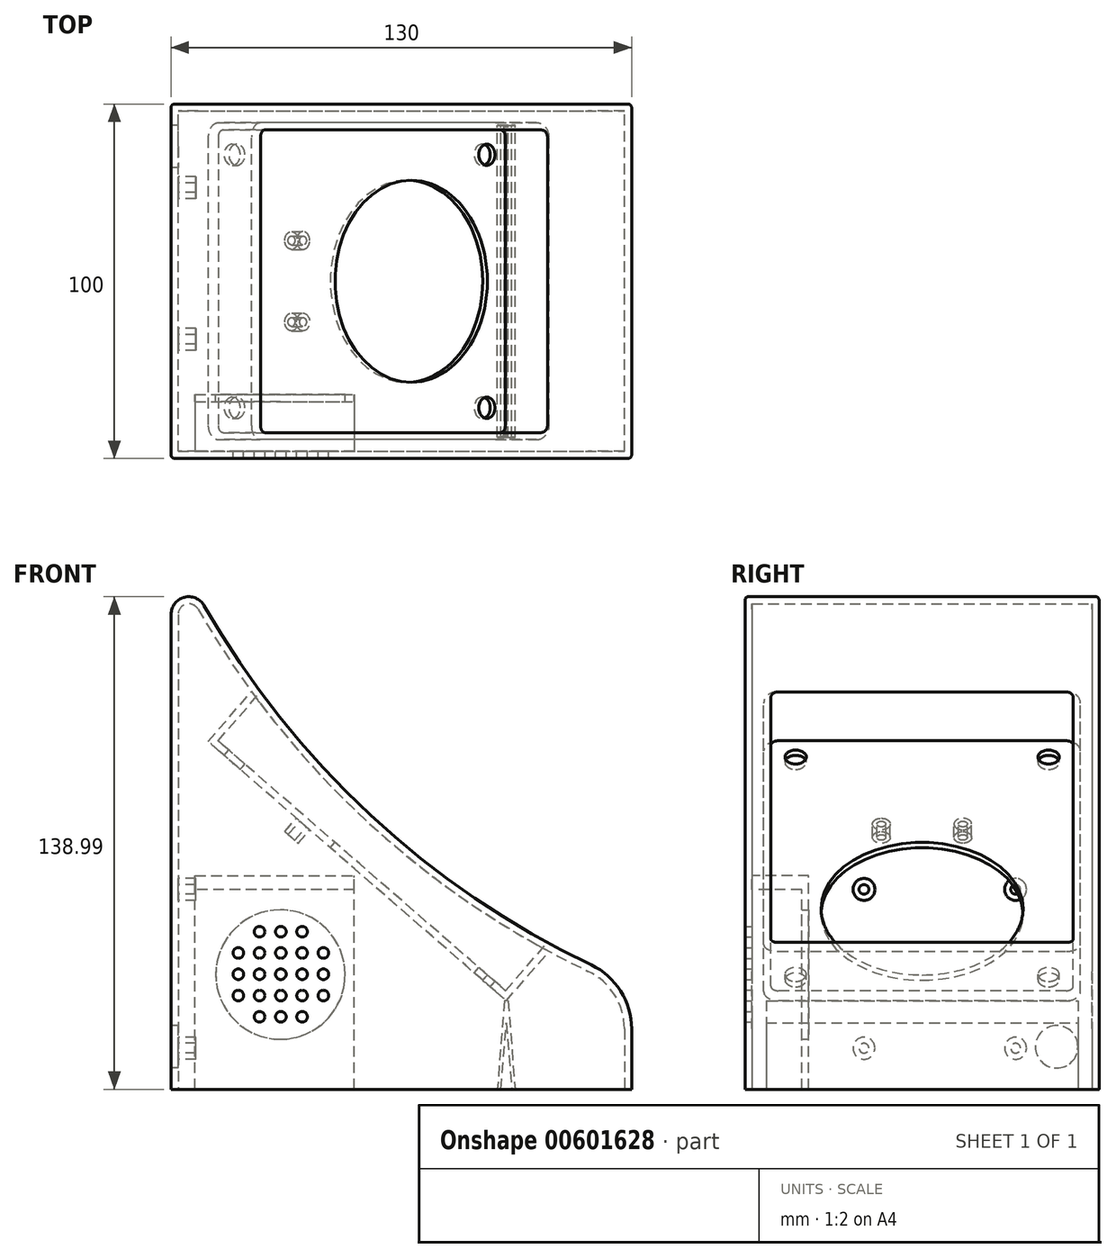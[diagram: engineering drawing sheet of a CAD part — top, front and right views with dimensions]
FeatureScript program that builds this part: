
annotation { "Feature Type Name" : "Feature", "Feature Type Description" : "" }
export const myFeature = defineFeature(function(context is Context, id is Id, definition is map)
    precondition{}
    {
        {
            var Q0;
            Q0=qCreatedBy(makeId("Front.planeOp"),FACE);
            var sketch = newSketch(context, id + "F0", { "sketchPlane" : qUnion([Q0])});
            skLineSegment(sketch, "E0", {"start": v(-84.02, -67.29) * mm, "end": v(45.98, -67.29) * mm});
            skPoint(sketch, "E1.visualSharp", {"position": v(-84.02, 87.14) * mm});
            skPoint(sketch, "E2.visualSharp", {"position": v(45.98, -37.29) * mm});
            skArc(sketch, "E3", {"start": v(-74.68, 69.19) * mm, "mid": v(-23.15, 5.98) * mm, "end": v(45.98, -37.29) * mm});
            skLineSegment(sketch, "E4", {"start": v(-84.02, 66.7) * mm, "end": v(-84.02, -67.29) * mm});
            skLineSegment(sketch, "E5", {"start": v(45.98, -37.29) * mm, "end": v(45.98, -67.29) * mm});
            skArc(sketch, "E6.filletArc", {"start": v(-74.68, 69.19) * mm, "mid": v(-80.3, 71.53) * mm, "end": v(-84.02, 66.7) * mm});
            skSolve(sketch);
        }
        {
            var Q0;
            Q0=makeQuery(id+"F0.imprint","IMPRINT",FACE,{"disambiguationData":[TD([[makeQuery(id+"F0.imprint","IMPRINT",EDGE,{"derivedFrom":sQuery(id+"F0.wireOp",EDGE,"E0")}),1.0]])]});
            extrude(context, id + "F1", {"entities" : qUnion([Q0]), "endBound" : BoundingType.SYMMETRIC, "depth" : 100 * mm});
        }
        {
            var Q0;
            Q0=makeQuery(id+"F1.opExtrude","SWEPT_EDGE",EDGE,{"disambiguationData":[OSD([sQuery(id+"F0.wireOp",EDGE,"E3"),sQuery(id+"F0.wireOp",EDGE,"E5")])]});
            cPlane(context, id + "F2", {"entities" : qUnion([Q0]), "cplaneType" : CPlaneType.LINE_ANGLE, "offset" : 25 * mm, "angle" : 41 * degree, "width" : 150 * mm, "height" : 150 * mm});
        }
        {
            var Q0;
            Q0=qCreatedBy(id+"F2.planeOp",FACE);
            var sketch = newSketch(context, id + "F3", { "sketchPlane" : qUnion([Q0])});
            skLineSegment(sketch, "E7.bottom", {"start": v(31.75, 42.7) * mm, "end": v(-71.75, 42.7) * mm});
            skLineSegment(sketch, "E7.top", {"start": v(31.75, -42.7) * mm, "end": v(-71.75, -42.7) * mm});
            skLineSegment(sketch, "E7.left", {"start": v(33.75, 40.7) * mm, "end": v(33.75, -40.7) * mm});
            skLineSegment(sketch, "E7.right", {"start": v(-73.75, 40.7) * mm, "end": v(-73.75, -40.7) * mm});
            skPoint(sketch, "E7.middle", {"position": v(-20, 0) * mm});
            skPoint(sketch, "E8.visualSharp", {"position": v(-73.75, -42.7) * mm});
            skArc(sketch, "E8.filletArc", {"start": v(-73.75, -40.7) * mm, "mid": v(-73.16, -42.11) * mm, "end": v(-71.75, -42.7) * mm});
            skPoint(sketch, "E9.visualSharp", {"position": v(-73.75, 42.7) * mm});
            skArc(sketch, "E9.filletArc", {"start": v(-71.75, 42.7) * mm, "mid": v(-73.16, 42.11) * mm, "end": v(-73.75, 40.7) * mm});
            skPoint(sketch, "E10.visualSharp", {"position": v(33.75, 42.7) * mm});
            skArc(sketch, "E10.filletArc", {"start": v(33.75, 40.7) * mm, "mid": v(33.16, 42.11) * mm, "end": v(31.75, 42.7) * mm});
            skPoint(sketch, "E11.visualSharp", {"position": v(33.75, -42.7) * mm});
            skArc(sketch, "E11.filletArc", {"start": v(31.75, -42.7) * mm, "mid": v(33.16, -42.11) * mm, "end": v(33.75, -40.7) * mm});
            skCircle(sketch, "E12", {"center": v(-1.55, 0) * mm, "radius": 28.5 * mm});
            skCircle(sketch, "E13", {"center": v(-66.75, -35.7) * mm, "radius": 3 * mm});
            skCircle(sketch, "E14", {"center": v(-66.75, 35.7) * mm, "radius": 3 * mm});
            skCircle(sketch, "E15", {"center": v(26.75, 35.7) * mm, "radius": 3 * mm});
            skCircle(sketch, "E16", {"center": v(26.75, -35.7) * mm, "radius": 3 * mm});
            skSolve(sketch);
        }
        {
            var Q0;
            Q0=makeQuery(id+"F3.imprint","IMPRINT",FACE,{"disambiguationData":[TD([[makeQuery(id+"F3.imprint","IMPRINT",EDGE,{"derivedFrom":sQuery(id+"F3.wireOp",EDGE,"E7.bottom")}),1.0]])]});
            var Q1;
            Q1=makeQuery(id+"F3.imprint","IMPRINT",FACE,{"disambiguationData":[TD([[makeQuery(id+"F3.imprint","IMPRINT",EDGE,{"derivedFrom":sQuery(id+"F3.wireOp",EDGE,"E12")}),1.0]])]});
            var Q2;
            Q2=makeQuery(id+"F3.imprint","IMPRINT",FACE,{"disambiguationData":[TD([[makeQuery(id+"F3.imprint","IMPRINT",EDGE,{"derivedFrom":sQuery(id+"F3.wireOp",EDGE,"E14")}),1.0]])]});
            var Q3;
            Q3=makeQuery(id+"F3.imprint","IMPRINT",FACE,{"disambiguationData":[TD([[makeQuery(id+"F3.imprint","IMPRINT",EDGE,{"derivedFrom":sQuery(id+"F3.wireOp",EDGE,"E15")}),1.0]])]});
            var Q4;
            Q4=makeQuery(id+"F3.imprint","IMPRINT",FACE,{"disambiguationData":[TD([[makeQuery(id+"F3.imprint","IMPRINT",EDGE,{"derivedFrom":sQuery(id+"F3.wireOp",EDGE,"E16")}),1.0]])]});
            var Q5;
            Q5=makeQuery(id+"F3.imprint","IMPRINT",FACE,{"disambiguationData":[TD([[makeQuery(id+"F3.imprint","IMPRINT",EDGE,{"derivedFrom":sQuery(id+"F3.wireOp",EDGE,"E13")}),1.0]])]});
            extrude(context, id + "F4", {"entities" : qUnion([Q0, Q1, Q2, Q3, Q4, Q5]), "operationType" : NewBodyOperationType.REMOVE, "oppositeDirection" : true, "depth" : 25 * mm});
        }
        {
            var Q0;
            Q0=makeQuery(id+"F1.opExtrude","SWEPT_EDGE",EDGE,{"disambiguationData":[OSD([sQuery(id+"F0.wireOp",EDGE,"E3"),sQuery(id+"F0.wireOp",EDGE,"E5")])]});
            fillet(context, id + "F5", {"entities" : qUnion([Q0]), "radius" : 20 * mm, "tangentPropagation" : true, "allowEdgeOverflow" : false});
        }
        {
            var Q0;
            Q0=makeQuery(id+"F1.opExtrude","SWEPT_FACE",FACE,{"disambiguationData":[OSD([sQuery(id+"F0.wireOp",EDGE,"E0")])]});
            shell(context, id + "F6", {"entities" : qUnion([Q0]), "thickness" : 2 * mm});
        }
        {
            var Q0;
            Q0=makeQuery(id+"F3.imprint","IMPRINT",FACE,{"disambiguationData":[TD([[makeQuery(id+"F3.imprint","IMPRINT",EDGE,{"derivedFrom":sQuery(id+"F3.wireOp",EDGE,"E12")}),1.0]])]});
            var Q1;
            Q1=makeQuery(id+"F3.imprint","IMPRINT",FACE,{"disambiguationData":[TD([[makeQuery(id+"F3.imprint","IMPRINT",EDGE,{"derivedFrom":sQuery(id+"F3.wireOp",EDGE,"E14")}),1.0]])]});
            var Q2;
            Q2=makeQuery(id+"F3.imprint","IMPRINT",FACE,{"disambiguationData":[TD([[makeQuery(id+"F3.imprint","IMPRINT",EDGE,{"derivedFrom":sQuery(id+"F3.wireOp",EDGE,"E13")}),1.0]])]});
            var Q3;
            Q3=makeQuery(id+"F3.imprint","IMPRINT",FACE,{"disambiguationData":[TD([[makeQuery(id+"F3.imprint","IMPRINT",EDGE,{"derivedFrom":sQuery(id+"F3.wireOp",EDGE,"E15")}),1.0]])]});
            var Q4;
            Q4=makeQuery(id+"F3.imprint","IMPRINT",FACE,{"disambiguationData":[TD([[makeQuery(id+"F3.imprint","IMPRINT",EDGE,{"derivedFrom":sQuery(id+"F3.wireOp",EDGE,"E16")}),1.0]])]});
            extrude(context, id + "F7", {"entities" : qUnion([Q0, Q1, Q2, Q3, Q4]), "operationType" : NewBodyOperationType.REMOVE, "oppositeDirection" : true, "depth" : 40 * mm});
        }
        {
            var Q0;
            Q0=makeQuery(id+"F1.opExtrude","SWEPT_FACE",FACE,{"disambiguationData":[OSD([sQuery(id+"F0.wireOp",EDGE,"E4")])]});
            var sketch = newSketch(context, id + "F8", { "sketchPlane" : qUnion([Q0])});
            skCircle(sketch, "E17", {"center": v(0, 42.55) * mm, "radius": 25 * mm, "construction": true});
            skLineSegment(sketch, "E18", {"start": v(0, 0) * mm, "end": v(0, -62.03) * mm, "construction": true});
            skLineSegment(sketch, "E19", {"start": v(-40.29, 42.55) * mm, "end": v(40.58, 42.55) * mm, "construction": true});
            skLineSegment(sketch, "E20", {"start": v(-40.29, 48.55) * mm, "end": v(40.58, 48.55) * mm, "construction": true});
            skLineSegment(sketch, "E21", {"start": v(-40.29, 36.55) * mm, "end": v(40.58, 36.55) * mm, "construction": true});
            skLineSegment(sketch, "E22", {"start": v(-40.29, 30.55) * mm, "end": v(40.58, 30.55) * mm, "construction": true});
            skLineSegment(sketch, "E23", {"start": v(-40.29, 54.55) * mm, "end": v(40.58, 54.55) * mm, "construction": true});
            skLineSegment(sketch, "E24", {"start": v(-6, 0) * mm, "end": v(-6, -62.03) * mm, "construction": true});
            skLineSegment(sketch, "E25", {"start": v(6, 0) * mm, "end": v(6, -62.03) * mm, "construction": true});
            skLineSegment(sketch, "E26", {"start": v(12, 0) * mm, "end": v(12, -62.03) * mm, "construction": true});
            skLineSegment(sketch, "E27", {"start": v(-12, 0) * mm, "end": v(-12, -62.03) * mm, "construction": true});
            skCircle(sketch, "E28", {"center": v(0, 42.55) * mm, "radius": 1.5 * mm});
            skCircle(sketch, "E29", {"center": v(6, 42.55) * mm, "radius": 1.5 * mm});
            skCircle(sketch, "E30", {"center": v(12, 42.55) * mm, "radius": 1.5 * mm});
            skCircle(sketch, "E31", {"center": v(-6, 42.55) * mm, "radius": 1.5 * mm});
            skCircle(sketch, "E32", {"center": v(-12, 42.55) * mm, "radius": 1.5 * mm});
            skCircle(sketch, "E33", {"center": v(0, 48.55) * mm, "radius": 1.5 * mm});
            skCircle(sketch, "E34", {"center": v(6, 48.55) * mm, "radius": 1.5 * mm});
            skCircle(sketch, "E35", {"center": v(-6, 48.55) * mm, "radius": 1.5 * mm});
            skCircle(sketch, "E36", {"center": v(-6, 54.55) * mm, "radius": 1.5 * mm});
            skCircle(sketch, "E37", {"center": v(0, 54.55) * mm, "radius": 1.5 * mm});
            skCircle(sketch, "E38", {"center": v(6, 54.55) * mm, "radius": 1.5 * mm});
            skCircle(sketch, "E39", {"center": v(12, 48.55) * mm, "radius": 1.5 * mm});
            skCircle(sketch, "E40", {"center": v(12, 36.55) * mm, "radius": 1.5 * mm});
            skCircle(sketch, "E41", {"center": v(6, 36.55) * mm, "radius": 1.5 * mm});
            skCircle(sketch, "E42", {"center": v(0, 36.55) * mm, "radius": 1.5 * mm});
            skCircle(sketch, "E43", {"center": v(-6, 36.55) * mm, "radius": 1.5 * mm});
            skCircle(sketch, "E44", {"center": v(-12, 36.55) * mm, "radius": 1.5 * mm});
            skCircle(sketch, "E45", {"center": v(-6, 30.55) * mm, "radius": 1.5 * mm});
            skCircle(sketch, "E46", {"center": v(0, 30.55) * mm, "radius": 1.5 * mm});
            skCircle(sketch, "E47", {"center": v(6, 30.55) * mm, "radius": 1.5 * mm});
            skCircle(sketch, "E48", {"center": v(-12, 48.55) * mm, "radius": 1.5 * mm});
            skCircle(sketch, "E49", {"center": v(-38, -55.29) * mm, "radius": 6 * mm});
            skLineSegment(sketch, "E50.bottom", {"start": v(42.5, -55.96) * mm, "end": v(-42.5, -55.96) * mm, "construction": true});
            skLineSegment(sketch, "E50.top", {"start": v(42.5, 0.04) * mm, "end": v(-42.5, 0.04) * mm, "construction": true});
            skLineSegment(sketch, "E50.left", {"start": v(42.5, -55.96) * mm, "end": v(42.5, 0.04) * mm, "construction": true});
            skLineSegment(sketch, "E50.right", {"start": v(-42.5, -55.96) * mm, "end": v(-42.5, 0.04) * mm, "construction": true});
            skPoint(sketch, "E50.middle", {"position": v(0, -27.96) * mm});
            skSolve(sketch);
        }
        {
            var Q0;
            Q0=makeQuery(id+"F8.imprint","IMPRINT",FACE,{"disambiguationData":[TD([[makeQuery(id+"F8.imprint","IMPRINT",EDGE,{"derivedFrom":sQuery(id+"F8.wireOp",EDGE,"E49")}),1.0]])]});
            extrude(context, id + "F9", {"entities" : qUnion([Q0]), "operationType" : NewBodyOperationType.REMOVE, "oppositeDirection" : true, "depth" : 25 * mm});
        }
        {
            var Q0;
            Q0=makeQuery(id+"F1.opExtrude","CAP_EDGE",EDGE,{"disambiguationData":[OSD([sQuery(id+"F0.wireOp",EDGE,"E3")])],"isStart":false});
            var Q1;
            Q1=makeQuery(id+"F1.opExtrude","CAP_EDGE",EDGE,{"disambiguationData":[OSD([sQuery(id+"F0.wireOp",EDGE,"E3")])],"isStart":true});
            fillet(context, id + "F10", {"entities" : qUnion([Q0, Q1]), "radius" : 1 * mm, "tangentPropagation" : true, "allowEdgeOverflow" : false});
        }
        {
            var Q0;
            Q0=makeQuery(id+"F6.opShell","OFFSET_FACE",FACE,{"disambiguationData":[OSD([sQuery(id+"F3.wireOp",EDGE,"E7.bottom"),sQuery(id+"F3.wireOp",EDGE,"E7.top"),sQuery(id+"F3.wireOp",EDGE,"E7.left"),sQuery(id+"F3.wireOp",EDGE,"E7.right"),sQuery(id+"F3.wireOp",EDGE,"E8.filletArc"),sQuery(id+"F3.wireOp",EDGE,"E9.filletArc"),sQuery(id+"F3.wireOp",EDGE,"E10.filletArc"),sQuery(id+"F3.wireOp",EDGE,"E11.filletArc")])]});
            cPlane(context, id + "F11", {"entities" : qUnion([Q0]), "cplaneType" : CPlaneType.OFFSET, "offset" : 0 * mm, "width" : 150 * mm, "height" : 150 * mm});
        }
        {
            var Q0;
            Q0=qCreatedBy(id+"F11.planeOp",FACE);
            var sketch = newSketch(context, id + "F12", { "sketchPlane" : qUnion([Q0])});
            skLineSegment(sketch, "E51.bottom", {"start": v(-38, 14) * mm, "end": v(-62, 14) * mm, "construction": true});
            skLineSegment(sketch, "E51.top", {"start": v(-38, -14) * mm, "end": v(-62, -14) * mm, "construction": true});
            skLineSegment(sketch, "E51.left", {"start": v(-38, 14) * mm, "end": v(-38, -14) * mm, "construction": true});
            skLineSegment(sketch, "E51.right", {"start": v(-62, 14) * mm, "end": v(-62, -14) * mm, "construction": true});
            skPoint(sketch, "E51.middle", {"position": v(-50, 0) * mm});
            skCircle(sketch, "E52", {"center": v(-40.24, 11.5) * mm, "radius": 1.25 * mm});
            skCircle(sketch, "E53", {"center": v(-40.24, -11.5) * mm, "radius": 1.25 * mm});
            skCircle(sketch, "E54", {"center": v(-40.24, 11.5) * mm, "radius": 2.5 * mm});
            skCircle(sketch, "E55", {"center": v(-40.24, -11.5) * mm, "radius": 2.5 * mm});
            skSolve(sketch);
        }
        {
            var Q0;
            {var subQ0=sQuery(id+"F0.wireOp",EDGE,"E6.filletArc");var subQ1=sQuery(id+"F0.wireOp",EDGE,"E5");var subQ2=sQuery(id+"F0.wireOp",EDGE,"E4");var subQ3=sQuery(id+"F0.wireOp",EDGE,"E3");var subQ4=sQuery(id+"F0.wireOp",EDGE,"E0");Q0=makeQuery(id+"F6.opShell","OFFSET_FACE",FACE,{"disambiguationData":[OSD([subQ4,subQ3,subQ2,subQ1,subQ0]),TDD([makeQuery(id+"F1.opExtrude","CAP_FACE",FACE,{"disambiguationData":[OSD([subQ4,subQ3,subQ2,subQ1,subQ0])],"isStart":false})])]});}
            var sketch = newSketch(context, id + "F13", { "sketchPlane" : qUnion([Q0])});
            skPoint(sketch, "E56.centerSnap0", {"position": v(36.97, -30.82) * mm});
            skCircle(sketch, "E57", {"center": v(53.03, -34.83) * mm, "radius": 1.5 * mm});
            skCircle(sketch, "E58", {"center": v(59.03, -34.83) * mm, "radius": 1.5 * mm});
            skCircle(sketch, "E59", {"center": v(65.03, -34.83) * mm, "radius": 1.5 * mm});
            skCircle(sketch, "E60", {"center": v(47.03, -34.83) * mm, "radius": 1.5 * mm});
            skCircle(sketch, "E61", {"center": v(41.03, -34.83) * mm, "radius": 1.5 * mm});
            skCircle(sketch, "E62", {"center": v(53.03, -28.83) * mm, "radius": 1.5 * mm});
            skCircle(sketch, "E63", {"center": v(59.03, -28.83) * mm, "radius": 1.5 * mm});
            skCircle(sketch, "E64", {"center": v(47.03, -28.83) * mm, "radius": 1.5 * mm});
            skCircle(sketch, "E65", {"center": v(47.03, -22.83) * mm, "radius": 1.5 * mm});
            skCircle(sketch, "E66", {"center": v(53.03, -22.83) * mm, "radius": 1.5 * mm});
            skCircle(sketch, "E67", {"center": v(59.03, -22.83) * mm, "radius": 1.5 * mm});
            skCircle(sketch, "E68", {"center": v(65.03, -28.83) * mm, "radius": 1.5 * mm});
            skCircle(sketch, "E69", {"center": v(65.03, -40.83) * mm, "radius": 1.5 * mm});
            skCircle(sketch, "E70", {"center": v(59.03, -40.83) * mm, "radius": 1.5 * mm});
            skCircle(sketch, "E71", {"center": v(53.03, -40.83) * mm, "radius": 1.5 * mm});
            skCircle(sketch, "E72", {"center": v(47.03, -40.83) * mm, "radius": 1.5 * mm});
            skCircle(sketch, "E73", {"center": v(41.03, -40.83) * mm, "radius": 1.5 * mm});
            skCircle(sketch, "E74", {"center": v(47.03, -46.83) * mm, "radius": 1.5 * mm});
            skCircle(sketch, "E75", {"center": v(53.03, -46.83) * mm, "radius": 1.5 * mm});
            skCircle(sketch, "E76", {"center": v(59.03, -46.83) * mm, "radius": 1.5 * mm});
            skCircle(sketch, "E77", {"center": v(41.03, -28.83) * mm, "radius": 1.5 * mm});
            skLineSegment(sketch, "E78", {"start": v(65.03, -40.83) * mm, "end": v(41.03, -40.83) * mm});
            skLineSegment(sketch, "E79", {"start": v(59.03, -46.83) * mm, "end": v(47.03, -46.83) * mm});
            skLineSegment(sketch, "E80", {"start": v(65.03, -28.83) * mm, "end": v(41.03, -28.83) * mm});
            skLineSegment(sketch, "E81", {"start": v(59.03, -22.83) * mm, "end": v(47.03, -22.83) * mm});
            skSolve(sketch);
        }
        {
            var Q0;
            {var subQ0=sQuery(id+"F13.wireOp",EDGE,"E80");var subQ1=sQuery(id+"F13.wireOp",EDGE,"E64");var subQ2=makeQuery(id+"F13.imprint","INTERSECT",VERTEX,{"disambiguationData":[OD(0.0)],"derivedFrom":[subQ1,subQ0]});Q0=makeQuery(id+"F13.imprint","IMPRINT",FACE,{"disambiguationData":[TD([[makeQuery(id+"F13.imprint","IMPRINT",EDGE,{"disambiguationData":[TD([[subQ2,-1.0]])],"derivedFrom":subQ1}),1.0]])]});}
            var Q1;
            {var subQ0=sQuery(id+"F13.wireOp",EDGE,"E78");var subQ1=sQuery(id+"F13.wireOp",EDGE,"E71");var subQ2=makeQuery(id+"F13.imprint","INTERSECT",VERTEX,{"disambiguationData":[OD(0.0)],"derivedFrom":[subQ1,subQ0]});Q1=makeQuery(id+"F13.imprint","IMPRINT",FACE,{"disambiguationData":[TD([[makeQuery(id+"F13.imprint","IMPRINT",EDGE,{"disambiguationData":[TD([[subQ2,1.0]])],"derivedFrom":subQ1}),1.0]])]});}
            var Q2;
            Q2=makeQuery(id+"F13.imprint","IMPRINT",FACE,{"disambiguationData":[TD([[makeQuery(id+"F13.imprint","IMPRINT",EDGE,{"derivedFrom":sQuery(id+"F13.wireOp",EDGE,"E59")}),1.0]])]});
            var Q3;
            Q3=makeQuery(id+"F13.imprint","IMPRINT",FACE,{"disambiguationData":[TD([[makeQuery(id+"F13.imprint","IMPRINT",EDGE,{"derivedFrom":sQuery(id+"F13.wireOp",EDGE,"E60")}),1.0]])]});
            var Q4;
            {var subQ0=sQuery(id+"F13.wireOp",EDGE,"E79");var subQ1=sQuery(id+"F13.wireOp",EDGE,"E75");var subQ2=makeQuery(id+"F13.imprint","INTERSECT",VERTEX,{"disambiguationData":[OD(0.0)],"derivedFrom":[subQ1,subQ0]});Q4=makeQuery(id+"F13.imprint","IMPRINT",FACE,{"disambiguationData":[TD([[makeQuery(id+"F13.imprint","IMPRINT",EDGE,{"disambiguationData":[TD([[subQ2,-1.0]])],"derivedFrom":subQ1}),1.0]])]});}
            var Q5;
            Q5=makeQuery(id+"F13.imprint","IMPRINT",FACE,{"disambiguationData":[TD([[makeQuery(id+"F13.imprint","IMPRINT",EDGE,{"derivedFrom":sQuery(id+"F13.wireOp",EDGE,"E58")}),1.0]])]});
            var Q6;
            Q6=makeQuery(id+"F13.imprint","IMPRINT",FACE,{"disambiguationData":[TD([[makeQuery(id+"F13.imprint","IMPRINT",EDGE,{"derivedFrom":sQuery(id+"F13.wireOp",EDGE,"E74")}),1.0]])]});
            var Q7;
            {var subQ0=sQuery(id+"F13.wireOp",EDGE,"E78");var subQ1=sQuery(id+"F13.wireOp",EDGE,"E71");var subQ2=makeQuery(id+"F13.imprint","INTERSECT",VERTEX,{"disambiguationData":[OD(0.0)],"derivedFrom":[subQ1,subQ0]});Q7=makeQuery(id+"F13.imprint","IMPRINT",FACE,{"disambiguationData":[TD([[makeQuery(id+"F13.imprint","IMPRINT",EDGE,{"disambiguationData":[TD([[subQ2,-1.0]])],"derivedFrom":subQ1}),1.0]])]});}
            var Q8;
            {var subQ0=sQuery(id+"F13.wireOp",EDGE,"E79");var subQ1=sQuery(id+"F13.wireOp",EDGE,"E75");var subQ2=makeQuery(id+"F13.imprint","INTERSECT",VERTEX,{"disambiguationData":[OD(0.0)],"derivedFrom":[subQ1,subQ0]});Q8=makeQuery(id+"F13.imprint","IMPRINT",FACE,{"disambiguationData":[TD([[makeQuery(id+"F13.imprint","IMPRINT",EDGE,{"disambiguationData":[TD([[subQ2,1.0]])],"derivedFrom":subQ1}),1.0]])]});}
            var Q9;
            {var subQ0=sQuery(id+"F13.wireOp",EDGE,"E80");var subQ1=sQuery(id+"F13.wireOp",EDGE,"E63");var subQ2=makeQuery(id+"F13.imprint","INTERSECT",VERTEX,{"disambiguationData":[OD(0.0)],"derivedFrom":[subQ1,subQ0]});Q9=makeQuery(id+"F13.imprint","IMPRINT",FACE,{"disambiguationData":[TD([[makeQuery(id+"F13.imprint","IMPRINT",EDGE,{"disambiguationData":[TD([[subQ2,-1.0]])],"derivedFrom":subQ1}),1.0]])]});}
            var Q10;
            {var subQ0=sQuery(id+"F13.wireOp",EDGE,"E81");var subQ1=sQuery(id+"F13.wireOp",EDGE,"E66");var subQ2=makeQuery(id+"F13.imprint","INTERSECT",VERTEX,{"disambiguationData":[OD(0.0)],"derivedFrom":[subQ1,subQ0]});Q10=makeQuery(id+"F13.imprint","IMPRINT",FACE,{"disambiguationData":[TD([[makeQuery(id+"F13.imprint","IMPRINT",EDGE,{"disambiguationData":[TD([[subQ2,1.0]])],"derivedFrom":subQ1}),1.0]])]});}
            var Q11;
            {var subQ0=sQuery(id+"F13.wireOp",EDGE,"E80");var subQ1=sQuery(id+"F13.wireOp",EDGE,"E64");var subQ2=makeQuery(id+"F13.imprint","INTERSECT",VERTEX,{"disambiguationData":[OD(0.0)],"derivedFrom":[subQ1,subQ0]});Q11=makeQuery(id+"F13.imprint","IMPRINT",FACE,{"disambiguationData":[TD([[makeQuery(id+"F13.imprint","IMPRINT",EDGE,{"disambiguationData":[TD([[subQ2,1.0]])],"derivedFrom":subQ1}),1.0]])]});}
            var Q12;
            Q12=makeQuery(id+"F13.imprint","IMPRINT",FACE,{"disambiguationData":[TD([[makeQuery(id+"F13.imprint","IMPRINT",EDGE,{"derivedFrom":sQuery(id+"F13.wireOp",EDGE,"E77")}),1.0]])]});
            var Q13;
            {var subQ0=sQuery(id+"F13.wireOp",EDGE,"E78");var subQ1=sQuery(id+"F13.wireOp",EDGE,"E72");var subQ2=makeQuery(id+"F13.imprint","INTERSECT",VERTEX,{"disambiguationData":[OD(0.0)],"derivedFrom":[subQ1,subQ0]});Q13=makeQuery(id+"F13.imprint","IMPRINT",FACE,{"disambiguationData":[TD([[makeQuery(id+"F13.imprint","IMPRINT",EDGE,{"disambiguationData":[TD([[subQ2,-1.0]])],"derivedFrom":subQ1}),1.0]])]});}
            var Q14;
            {var subQ0=sQuery(id+"F13.wireOp",EDGE,"E78");var subQ1=sQuery(id+"F13.wireOp",EDGE,"E70");var subQ2=makeQuery(id+"F13.imprint","INTERSECT",VERTEX,{"disambiguationData":[OD(0.0)],"derivedFrom":[subQ1,subQ0]});Q14=makeQuery(id+"F13.imprint","IMPRINT",FACE,{"disambiguationData":[TD([[makeQuery(id+"F13.imprint","IMPRINT",EDGE,{"disambiguationData":[TD([[subQ2,1.0]])],"derivedFrom":subQ1}),1.0]])]});}
            var Q15;
            {var subQ0=sQuery(id+"F13.wireOp",EDGE,"E80");var subQ1=sQuery(id+"F13.wireOp",EDGE,"E62");var subQ2=makeQuery(id+"F13.imprint","INTERSECT",VERTEX,{"disambiguationData":[OD(0.0)],"derivedFrom":[subQ1,subQ0]});Q15=makeQuery(id+"F13.imprint","IMPRINT",FACE,{"disambiguationData":[TD([[makeQuery(id+"F13.imprint","IMPRINT",EDGE,{"disambiguationData":[TD([[subQ2,1.0]])],"derivedFrom":subQ1}),1.0]])]});}
            var Q16;
            Q16=makeQuery(id+"F13.imprint","IMPRINT",FACE,{"disambiguationData":[TD([[makeQuery(id+"F13.imprint","IMPRINT",EDGE,{"derivedFrom":sQuery(id+"F13.wireOp",EDGE,"E67")}),1.0]])]});
            var Q17;
            {var subQ0=sQuery(id+"F13.wireOp",EDGE,"E80");var subQ1=sQuery(id+"F13.wireOp",EDGE,"E63");var subQ2=makeQuery(id+"F13.imprint","INTERSECT",VERTEX,{"disambiguationData":[OD(0.0)],"derivedFrom":[subQ1,subQ0]});Q17=makeQuery(id+"F13.imprint","IMPRINT",FACE,{"disambiguationData":[TD([[makeQuery(id+"F13.imprint","IMPRINT",EDGE,{"disambiguationData":[TD([[subQ2,1.0]])],"derivedFrom":subQ1}),1.0]])]});}
            var Q18;
            Q18=makeQuery(id+"F13.imprint","IMPRINT",FACE,{"disambiguationData":[TD([[makeQuery(id+"F13.imprint","IMPRINT",EDGE,{"derivedFrom":sQuery(id+"F13.wireOp",EDGE,"E65")}),1.0]])]});
            var Q19;
            {var subQ0=sQuery(id+"F13.wireOp",EDGE,"E78");var subQ1=sQuery(id+"F13.wireOp",EDGE,"E70");var subQ2=makeQuery(id+"F13.imprint","INTERSECT",VERTEX,{"disambiguationData":[OD(0.0)],"derivedFrom":[subQ1,subQ0]});Q19=makeQuery(id+"F13.imprint","IMPRINT",FACE,{"disambiguationData":[TD([[makeQuery(id+"F13.imprint","IMPRINT",EDGE,{"disambiguationData":[TD([[subQ2,-1.0]])],"derivedFrom":subQ1}),1.0]])]});}
            var Q20;
            Q20=makeQuery(id+"F13.imprint","IMPRINT",FACE,{"disambiguationData":[TD([[makeQuery(id+"F13.imprint","IMPRINT",EDGE,{"derivedFrom":sQuery(id+"F13.wireOp",EDGE,"E76")}),1.0]])]});
            var Q21;
            Q21=makeQuery(id+"F13.imprint","IMPRINT",FACE,{"disambiguationData":[TD([[makeQuery(id+"F13.imprint","IMPRINT",EDGE,{"derivedFrom":sQuery(id+"F13.wireOp",EDGE,"E57")}),1.0]])]});
            var Q22;
            Q22=makeQuery(id+"F13.imprint","IMPRINT",FACE,{"disambiguationData":[TD([[makeQuery(id+"F13.imprint","IMPRINT",EDGE,{"derivedFrom":sQuery(id+"F13.wireOp",EDGE,"E73")}),1.0]])]});
            var Q23;
            Q23=makeQuery(id+"F13.imprint","IMPRINT",FACE,{"disambiguationData":[TD([[makeQuery(id+"F13.imprint","IMPRINT",EDGE,{"derivedFrom":sQuery(id+"F13.wireOp",EDGE,"E61")}),1.0]])]});
            var Q24;
            {var subQ0=sQuery(id+"F13.wireOp",EDGE,"E78");var subQ1=sQuery(id+"F13.wireOp",EDGE,"E72");var subQ2=makeQuery(id+"F13.imprint","INTERSECT",VERTEX,{"disambiguationData":[OD(0.0)],"derivedFrom":[subQ1,subQ0]});Q24=makeQuery(id+"F13.imprint","IMPRINT",FACE,{"disambiguationData":[TD([[makeQuery(id+"F13.imprint","IMPRINT",EDGE,{"disambiguationData":[TD([[subQ2,1.0]])],"derivedFrom":subQ1}),1.0]])]});}
            var Q25;
            {var subQ0=sQuery(id+"F13.wireOp",EDGE,"E80");var subQ1=sQuery(id+"F13.wireOp",EDGE,"E62");var subQ2=makeQuery(id+"F13.imprint","INTERSECT",VERTEX,{"disambiguationData":[OD(0.0)],"derivedFrom":[subQ1,subQ0]});Q25=makeQuery(id+"F13.imprint","IMPRINT",FACE,{"disambiguationData":[TD([[makeQuery(id+"F13.imprint","IMPRINT",EDGE,{"disambiguationData":[TD([[subQ2,-1.0]])],"derivedFrom":subQ1}),1.0]])]});}
            var Q26;
            {var subQ0=sQuery(id+"F13.wireOp",EDGE,"E81");var subQ1=sQuery(id+"F13.wireOp",EDGE,"E66");var subQ2=makeQuery(id+"F13.imprint","INTERSECT",VERTEX,{"disambiguationData":[OD(0.0)],"derivedFrom":[subQ1,subQ0]});Q26=makeQuery(id+"F13.imprint","IMPRINT",FACE,{"disambiguationData":[TD([[makeQuery(id+"F13.imprint","IMPRINT",EDGE,{"disambiguationData":[TD([[subQ2,-1.0]])],"derivedFrom":subQ1}),1.0]])]});}
            var Q27;
            Q27=makeQuery(id+"F13.imprint","IMPRINT",FACE,{"disambiguationData":[TD([[makeQuery(id+"F13.imprint","IMPRINT",EDGE,{"derivedFrom":sQuery(id+"F13.wireOp",EDGE,"E69")}),1.0]])]});
            var Q28;
            Q28=makeQuery(id+"F13.imprint","IMPRINT",FACE,{"disambiguationData":[TD([[makeQuery(id+"F13.imprint","IMPRINT",EDGE,{"derivedFrom":sQuery(id+"F13.wireOp",EDGE,"E68")}),1.0]])]});
            var Q29;
            Q29=sQuery(id+"F13.wireOp",EDGE,"E81");
            var Q30;
            Q30=sQuery(id+"F13.wireOp",EDGE,"E67");
            var Q31;
            Q31=sQuery(id+"F13.wireOp",EDGE,"E65");
            var Q32;
            Q32=sQuery(id+"F13.wireOp",EDGE,"E63");
            var Q33;
            Q33=sQuery(id+"F13.wireOp",EDGE,"E58");
            var Q34;
            Q34=sQuery(id+"F13.wireOp",EDGE,"E80");
            var Q35;
            Q35=sQuery(id+"F13.wireOp",EDGE,"E78");
            var Q36;
            Q36=sQuery(id+"F13.wireOp",EDGE,"E79");
            var Q37;
            Q37=sQuery(id+"F13.wireOp",EDGE,"E70");
            var Q38;
            Q38=sQuery(id+"F13.wireOp",EDGE,"E73");
            var Q39;
            Q39=sQuery(id+"F13.wireOp",EDGE,"E72");
            var Q40;
            Q40=sQuery(id+"F13.wireOp",EDGE,"E64");
            var Q41;
            Q41=sQuery(id+"F13.wireOp",EDGE,"E76");
            var Q42;
            Q42=sQuery(id+"F13.wireOp",EDGE,"E59");
            var Q43;
            Q43=sQuery(id+"F13.wireOp",EDGE,"E57");
            var Q44;
            Q44=sQuery(id+"F13.wireOp",EDGE,"E71");
            var Q45;
            Q45=sQuery(id+"F13.wireOp",EDGE,"E77");
            var Q46;
            Q46=sQuery(id+"F13.wireOp",EDGE,"E74");
            var Q47;
            Q47=sQuery(id+"F13.wireOp",EDGE,"E68");
            var Q48;
            Q48=sQuery(id+"F13.wireOp",EDGE,"E69");
            var Q49;
            Q49=sQuery(id+"F13.wireOp",EDGE,"E75");
            var Q50;
            Q50=sQuery(id+"F13.wireOp",EDGE,"E66");
            var Q51;
            Q51=sQuery(id+"F13.wireOp",EDGE,"E61");
            var Q52;
            Q52=sQuery(id+"F13.wireOp",EDGE,"E60");
            var Q53;
            Q53=sQuery(id+"F13.wireOp",EDGE,"E62");
            extrude(context, id + "F14", {"entities" : qUnion([Q0, Q1, Q2, Q3, Q4, Q5, Q6, Q7, Q8, Q9, Q10, Q11, Q12, Q13, Q14, Q15, Q16, Q17, Q18, Q19, Q20, Q21, Q22, Q23, Q24, Q25, Q26, Q27, Q28]), "operationType" : NewBodyOperationType.REMOVE, "surfaceEntities" : qUnion([Q29, Q30, Q31, Q32, Q33, Q34, Q35, Q36, Q37, Q38, Q39, Q40, Q41, Q42, Q43, Q44, Q45, Q46, Q47, Q48, Q49, Q50, Q51, Q52, Q53]), "oppositeDirection" : true, "depth" : 25 * mm});
        }
        {
            var Q0;
            {var subQ0=sQuery(id+"F0.wireOp",EDGE,"E6.filletArc");var subQ1=sQuery(id+"F0.wireOp",EDGE,"E5");var subQ2=sQuery(id+"F0.wireOp",EDGE,"E4");var subQ3=sQuery(id+"F0.wireOp",EDGE,"E3");var subQ4=sQuery(id+"F0.wireOp",EDGE,"E0");Q0=makeQuery(id+"F6.opShell","OFFSET_FACE",FACE,{"disambiguationData":[OSD([subQ4,subQ3,subQ2,subQ1,subQ0]),TDD([makeQuery(id+"F1.opExtrude","CAP_FACE",FACE,{"disambiguationData":[OSD([subQ4,subQ3,subQ2,subQ1,subQ0])],"isStart":false})])]});}
            var sketch = newSketch(context, id + "F15", { "sketchPlane" : qUnion([Q0])});
            skLineSegment(sketch, "E82.top", {"start": v(77.3, -7) * mm, "end": v(32.3, -7) * mm});
            skLineSegment(sketch, "E82.left", {"start": v(77.3, -11) * mm, "end": v(77.3, -7) * mm});
            skLineSegment(sketch, "E82.right", {"start": v(32.3, -11) * mm, "end": v(32.3, -7) * mm});
            skPoint(sketch, "E82.middle", {"position": v(54.8, -9) * mm});
            skLineSegment(sketch, "E83", {"start": v(77.3, -11) * mm, "end": v(77.3, -56) * mm, "construction": true});
            skLineSegment(sketch, "E84", {"start": v(77.3, -33.5) * mm, "end": v(33.54, -33.5) * mm, "construction": true});
            skLineSegment(sketch, "E85", {"start": v(32.3, -11) * mm, "end": v(77.3, -11) * mm});
            skSolve(sketch);
        }
        {
            var Q0;
            Q0=qSketchRegion(id+"F15",true);
            extrude(context, id + "F16", {"entities" : qUnion([Q0]), "operationType" : NewBodyOperationType.ADD, "depth" : 16 * mm});
        }
        {
            var Q0;
            Q0=makeQuery(id+"F16.opExtrude","SWEPT_FACE",FACE,{"disambiguationData":[OSD([sQuery(id+"F15.wireOp",EDGE,"E85")])]});
            var sketch = newSketch(context, id + "F17", { "sketchPlane" : qUnion([Q0])});
            skLineSegment(sketch, "E86.bottom", {"start": v(-77.3, 32) * mm, "end": v(-32.3, 32) * mm});
            skLineSegment(sketch, "E86.top", {"start": v(-77.3, 34) * mm, "end": v(-32.3, 34) * mm});
            skLineSegment(sketch, "E86.left", {"start": v(-77.3, 32) * mm, "end": v(-77.3, 34) * mm});
            skLineSegment(sketch, "E86.right", {"start": v(-32.3, 32) * mm, "end": v(-32.3, 34) * mm});
            skSolve(sketch);
        }
        {
            var Q0;
            Q0=makeQuery(id+"F17.imprint","IMPRINT",FACE,{"disambiguationData":[TD([[makeQuery(id+"F17.imprint","IMPRINT",EDGE,{"derivedFrom":sQuery(id+"F17.wireOp",EDGE,"E86.bottom")}),-1.0]])]});
            var Q1;
            Q1=makeQuery(id+"F1.opExtrude","SWEPT_FACE",FACE,{"disambiguationData":[OSD([sQuery(id+"F0.wireOp",EDGE,"E0")])]});
            extrude(context, id + "F18", {"entities" : qUnion([Q0]), "operationType" : NewBodyOperationType.ADD, "endBound" : BoundingType.UP_TO_SURFACE, "endBoundEntityFace" : qUnion([Q1]), "depth" : 50 * mm});
        }
        {
            var Q0;
            Q0=makeQuery(id+"F18.boolean.opBoolean","MERGE",FACE,{"derivedFrom":[makeQuery(id+"F16.opExtrude","CAP_FACE",FACE,{"disambiguationData":[OSD([sQuery(id+"F15.wireOp",EDGE,"E82.bottom"),sQuery(id+"F15.wireOp",EDGE,"E82.top"),sQuery(id+"F15.wireOp",EDGE,"E82.left"),sQuery(id+"F15.wireOp",EDGE,"E82.right")])],"isStart":false}),makeQuery(id+"F18.opExtrude","SWEPT_FACE",FACE,{"disambiguationData":[OSD([sQuery(id+"F17.wireOp",EDGE,"CFtCSqfR-IfQe-7JBa-NznS-rNRl7jurEekL.bottom")])]})]});
            var sketch = newSketch(context, id + "F19", { "sketchPlane" : qUnion([Q0])});
            skCircle(sketch, "E87", {"center": v(53.14, -34.91) * mm, "radius": 18.25 * mm});
            skSolve(sketch);
        }
        {
            var Q0;
            Q0=makeQuery(id+"F19.imprint","IMPRINT",FACE,{"disambiguationData":[TD([[makeQuery(id+"F19.imprint","IMPRINT",EDGE,{"derivedFrom":sQuery(id+"F19.wireOp",EDGE,"E87")}),1.0]])]});
            var Q1;
            Q1=sQuery(id+"F19.wireOp",EDGE,"E87");
            extrude(context, id + "F20", {"entities" : qUnion([Q0]), "operationType" : NewBodyOperationType.REMOVE, "surfaceEntities" : qUnion([Q1]), "oppositeDirection" : true, "depth" : 5 * mm});
        }
        {
            var Q0;
            Q0=makeQuery(id+"F6.opShell","OFFSET_FACE",FACE,{"disambiguationData":[OSD([sQuery(id+"F0.wireOp",EDGE,"E4")])]});
            var sketch = newSketch(context, id + "F21", { "sketchPlane" : qUnion([Q0])});
            skLineSegment(sketch, "E88.bottom", {"start": v(-23, -62.29) * mm, "end": v(33, -62.29) * mm, "construction": true});
            skLineSegment(sketch, "E88.top", {"start": v(-23, 22.71) * mm, "end": v(33, 22.71) * mm, "construction": true});
            skLineSegment(sketch, "E88.left", {"start": v(-23, -62.29) * mm, "end": v(-23, 22.71) * mm, "construction": true});
            skLineSegment(sketch, "E88.right", {"start": v(33, -62.29) * mm, "end": v(33, 22.71) * mm, "construction": true});
            skCircle(sketch, "E89", {"center": v(26.4, -55.69) * mm, "radius": 3.1 * mm});
            skCircle(sketch, "E90", {"center": v(26.4, -55.69) * mm, "radius": 1.38 * mm});
            skCircle(sketch, "E91", {"center": v(-16.4, -55.69) * mm, "radius": 3.1 * mm});
            skCircle(sketch, "E92", {"center": v(-16.4, -55.69) * mm, "radius": 1.38 * mm});
            skCircle(sketch, "E93", {"center": v(-16.4, -10.89) * mm, "radius": 3.1 * mm});
            skCircle(sketch, "E94", {"center": v(-16.4, -10.89) * mm, "radius": 1.37 * mm});
            skCircle(sketch, "E95", {"center": v(26.4, -10.89) * mm, "radius": 3.1 * mm});
            skCircle(sketch, "E96", {"center": v(26.4, -10.89) * mm, "radius": 1.38 * mm});
            skLineSegment(sketch, "E97", {"start": v(43.64, -4.29) * mm, "end": v(-31, -4.29) * mm, "construction": true});
            skSolve(sketch);
        }
        {
            var Q0;
            Q0=makeQuery(id+"F21.imprint","IMPRINT",FACE,{"disambiguationData":[TD([[makeQuery(id+"F21.imprint","IMPRINT",EDGE,{"derivedFrom":sQuery(id+"F21.wireOp",EDGE,"E91")}),1.0]])]});
            var Q1;
            Q1=makeQuery(id+"F21.imprint","IMPRINT",FACE,{"disambiguationData":[TD([[makeQuery(id+"F21.imprint","IMPRINT",EDGE,{"derivedFrom":sQuery(id+"F21.wireOp",EDGE,"E93")}),1.0]])]});
            var Q2;
            Q2=makeQuery(id+"F21.imprint","IMPRINT",FACE,{"disambiguationData":[TD([[makeQuery(id+"F21.imprint","IMPRINT",EDGE,{"derivedFrom":sQuery(id+"F21.wireOp",EDGE,"E95")}),1.0]])]});
            var Q3;
            Q3=makeQuery(id+"F21.imprint","IMPRINT",FACE,{"disambiguationData":[TD([[makeQuery(id+"F21.imprint","IMPRINT",EDGE,{"derivedFrom":sQuery(id+"F21.wireOp",EDGE,"E89")}),1.0]])]});
            extrude(context, id + "F22", {"entities" : qUnion([Q0, Q1, Q2, Q3]), "operationType" : NewBodyOperationType.ADD, "depth" : 5 * mm});
        }
        {
            var Q0;
            Q0=makeQuery(id+"F1.opExtrude","CAP_FACE",FACE,{"disambiguationData":[OSD([sQuery(id+"F0.wireOp",EDGE,"E0"),sQuery(id+"F0.wireOp",EDGE,"E3"),sQuery(id+"F0.wireOp",EDGE,"E4"),sQuery(id+"F0.wireOp",EDGE,"E5"),sQuery(id+"F0.wireOp",EDGE,"E6.filletArc")])],"isStart":true});
            cPlane(context, id + "F23", {"entities" : qUnion([Q0]), "cplaneType" : CPlaneType.OFFSET, "offset" : 6 * mm, "oppositeDirection" : true, "width" : 150 * mm, "height" : 150 * mm});
        }
        {
            var Q0;
            Q0=qCreatedBy(id+"F23.planeOp",FACE);
            var sketch = newSketch(context, id + "F24", { "sketchPlane" : qUnion([Q0])});
            skLineSegment(sketch, "E98", {"start": v(-11.1, -42.3) * mm, "end": v(-10.1, -42.3) * mm});
            skLineSegment(sketch, "E99", {"start": v(-11.1, -42.3) * mm, "end": v(-13.1, -67.29) * mm});
            skLineSegment(sketch, "E100", {"start": v(-10.1, -42.3) * mm, "end": v(-8.1, -67.29) * mm});
            skLineSegment(sketch, "E101", {"start": v(-13.1, -67.29) * mm, "end": v(-12.1, -67.29) * mm});
            skLineSegment(sketch, "E102", {"start": v(-8.1, -67.29) * mm, "end": v(-9.1, -67.29) * mm});
            skLineSegment(sketch, "E103", {"start": v(-9.1, -67.29) * mm, "end": v(-10.6, -48.55) * mm});
            skLineSegment(sketch, "E104", {"start": v(-10.6, -48.55) * mm, "end": v(-12.1, -67.29) * mm});
            skSolve(sketch);
        }
        {
            var Q0;
            Q0=makeQuery(id+"F24.imprint","IMPRINT",FACE,{"disambiguationData":[TD([[makeQuery(id+"F24.imprint","IMPRINT",EDGE,{"derivedFrom":sQuery(id+"F24.wireOp",EDGE,"E98")}),-1.0]])]});
            extrude(context, id + "F25", {"entities" : qUnion([Q0]), "oppositeDirection" : true, "depth" : 88 * mm});
        }
        {
            var Q0;
            Q0=makeQuery(id+"F12.imprint","IMPRINT",FACE,{"disambiguationData":[TD([[makeQuery(id+"F12.imprint","IMPRINT",EDGE,{"derivedFrom":sQuery(id+"F12.wireOp",EDGE,"E52")}),-1.0]])]});
            var Q1;
            Q1=makeQuery(id+"F12.imprint","IMPRINT",FACE,{"disambiguationData":[TD([[makeQuery(id+"F12.imprint","IMPRINT",EDGE,{"derivedFrom":sQuery(id+"F12.wireOp",EDGE,"E53")}),-1.0]])]});
            extrude(context, id + "F26", {"entities" : qUnion([Q0, Q1]), "operationType" : NewBodyOperationType.ADD, "depth" : 5 * mm});
        }
        {
            var Q0;
            Q0=makeQuery(id+"F21.imprint","IMPRINT",FACE,{"disambiguationData":[TD([[makeQuery(id+"F21.imprint","IMPRINT",EDGE,{"derivedFrom":sQuery(id+"F21.wireOp",EDGE,"E89")}),-1.0]])]});
            cPlane(context, id + "F27", {"entities" : qUnion([Q0]), "cplaneType" : CPlaneType.OFFSET, "offset" : 5 * mm, "width" : 150 * mm, "height" : 150 * mm});
        }
    });
